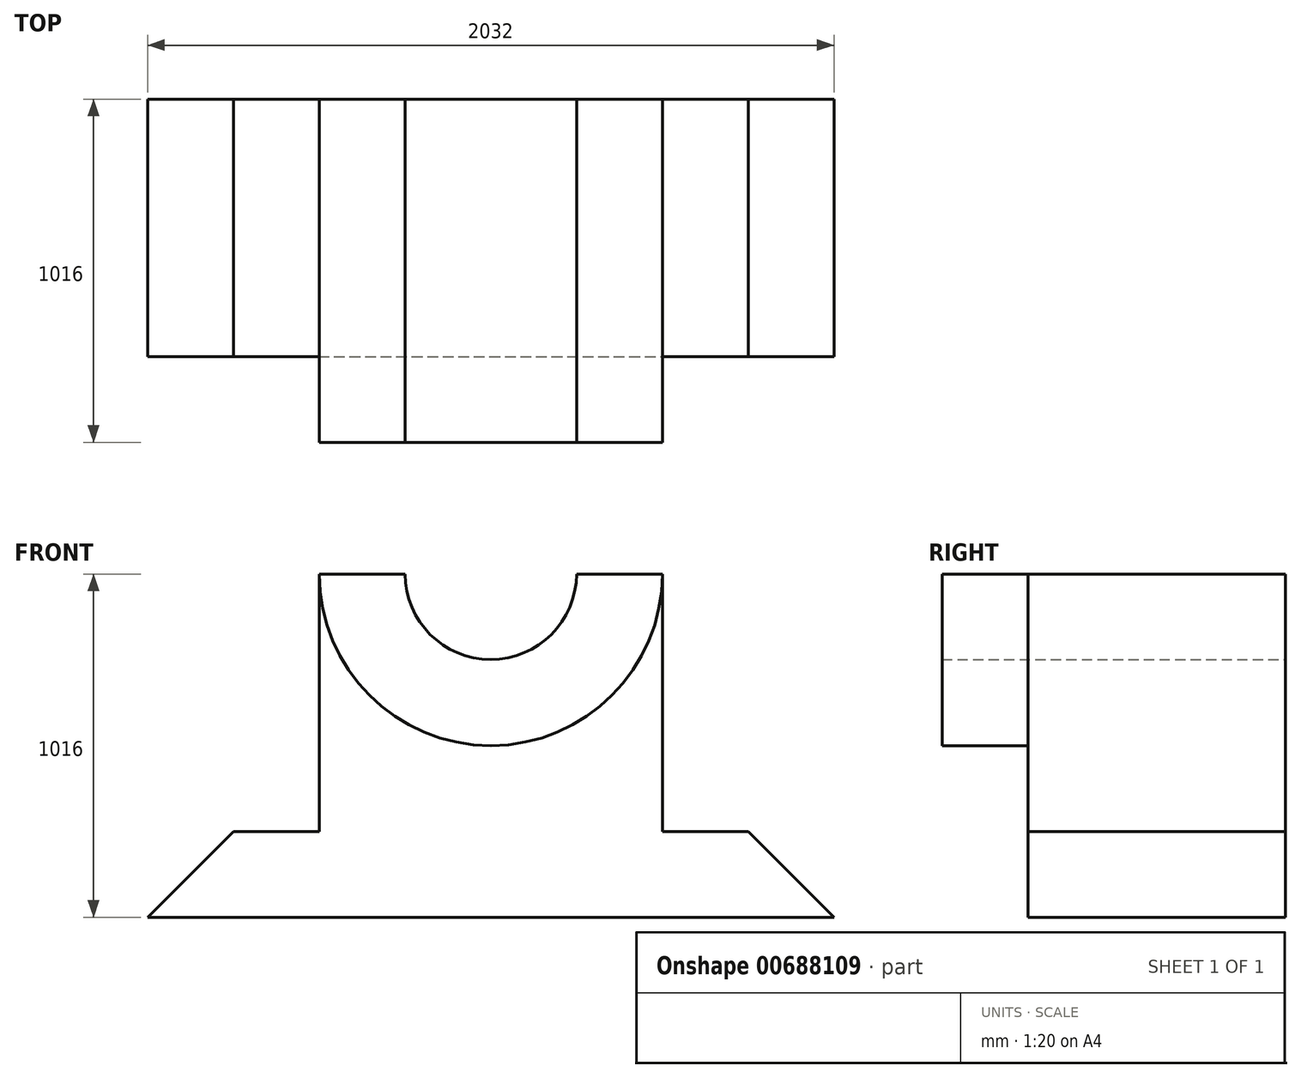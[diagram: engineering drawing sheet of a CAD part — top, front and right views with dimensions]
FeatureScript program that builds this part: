
annotation { "Feature Type Name" : "Feature", "Feature Type Description" : "" }
export const myFeature = defineFeature(function(context is Context, id is Id, definition is map)
    precondition{}
    {
        {
            var Q0;
            Q0=qCreatedBy(makeId("Front.planeOp"),FACE);
            var sketch = newSketch(context, id + "F0", { "sketchPlane" : qUnion([Q0])});
            skLineSegment(sketch, "E0", {"start": v(0, 0) * mm, "end": v(2032, 0) * mm});
            skLineSegment(sketch, "E1", {"start": v(2032, 0) * mm, "end": v(1778, 254) * mm});
            skLineSegment(sketch, "E2", {"start": v(1778, 254) * mm, "end": v(1524, 254) * mm});
            skLineSegment(sketch, "E3", {"start": v(1524, 254) * mm, "end": v(1524, 1016) * mm});
            skLineSegment(sketch, "E4", {"start": v(1524, 1016) * mm, "end": v(508, 1016) * mm});
            skLineSegment(sketch, "E5", {"start": v(508, 1016) * mm, "end": v(508, 254) * mm});
            skLineSegment(sketch, "E6", {"start": v(508, 254) * mm, "end": v(254, 254) * mm});
            skLineSegment(sketch, "E7", {"start": v(254, 254) * mm, "end": v(0, 0) * mm});
            skSolve(sketch);
        }
        {
            var Q0;
            Q0=makeQuery(id+"F0.imprint","IMPRINT",FACE,{"disambiguationData":[TD([[makeQuery(id+"F0.imprint","IMPRINT",EDGE,{"derivedFrom":sQuery(id+"F0.wireOp",EDGE,"E0")}),1.0]])]});
            extrude(context, id + "F1", {"entities" : qUnion([Q0]), "depth" : 762 * mm, "offsetDistance" : 25.4 * mm});
        }
        {
            var Q0;
            Q0=makeQuery(id+"F1.opExtrude","CAP_FACE",FACE,{"disambiguationData":[OSD([sQuery(id+"F0.wireOp",EDGE,"E0"),sQuery(id+"F0.wireOp",EDGE,"E1"),sQuery(id+"F0.wireOp",EDGE,"E2"),sQuery(id+"F0.wireOp",EDGE,"E3"),sQuery(id+"F0.wireOp",EDGE,"E4"),sQuery(id+"F0.wireOp",EDGE,"E5"),sQuery(id+"F0.wireOp",EDGE,"E6"),sQuery(id+"F0.wireOp",EDGE,"E7")])],"isStart":false});
            var sketch = newSketch(context, id + "F2", { "sketchPlane" : qUnion([Q0])});
            skLineSegment(sketch, "E8", {"start": v(508, 1016) * mm, "end": v(762, 1016) * mm});
            skLineSegment(sketch, "E9", {"start": v(1524, 1016) * mm, "end": v(1270, 1016) * mm});
            skArc(sketch, "E10", {"start": v(762, 1016) * mm, "mid": v(1016, 762.94) * mm, "end": v(1270, 1016) * mm});
            skArc(sketch, "E11", {"start": v(508, 1016) * mm, "mid": v(1016, 508) * mm, "end": v(1524, 1016) * mm});
            skSolve(sketch);
        }
        {
            var Q0;
            Q0=makeQuery(id+"F2.imprint","IMPRINT",FACE,{"disambiguationData":[TD([[makeQuery(id+"F2.imprint","IMPRINT",EDGE,{"derivedFrom":sQuery(id+"F2.wireOp",EDGE,"E8")}),1.0]])]});
            extrude(context, id + "F3", {"entities" : qUnion([Q0]), "operationType" : NewBodyOperationType.ADD, "depth" : 254 * mm, "offsetDistance" : 25.4 * mm});
        }
        {
            var Q0;
            {var subQ0=sQuery(id+"F0.wireOp",EDGE,"E4");Q0=makeQuery(id+"F3.boolean.opBoolean","SPLIT",FACE,{"disambiguationData":[TD([makeQuery(id+"F3.opExtrude","SWEPT_FACE",FACE,{"disambiguationData":[OSD([sQuery(id+"F2.wireOp",EDGE,"E10")])]})])],"derivedFrom":makeQuery(id+"F1.opExtrude","CAP_FACE",FACE,{"disambiguationData":[OSD([sQuery(id+"F0.wireOp",EDGE,"E0"),sQuery(id+"F0.wireOp",EDGE,"E1"),sQuery(id+"F0.wireOp",EDGE,"E2"),sQuery(id+"F0.wireOp",EDGE,"E3"),subQ0,sQuery(id+"F0.wireOp",EDGE,"E5"),sQuery(id+"F0.wireOp",EDGE,"E6"),sQuery(id+"F0.wireOp",EDGE,"E7")])],"isStart":false})});}
            extrude(context, id + "F4", {"entities" : qUnion([Q0]), "operationType" : NewBodyOperationType.REMOVE, "oppositeDirection" : true, "depth" : 1143 * mm, "offsetDistance" : 25.4 * mm});
        }
    });
